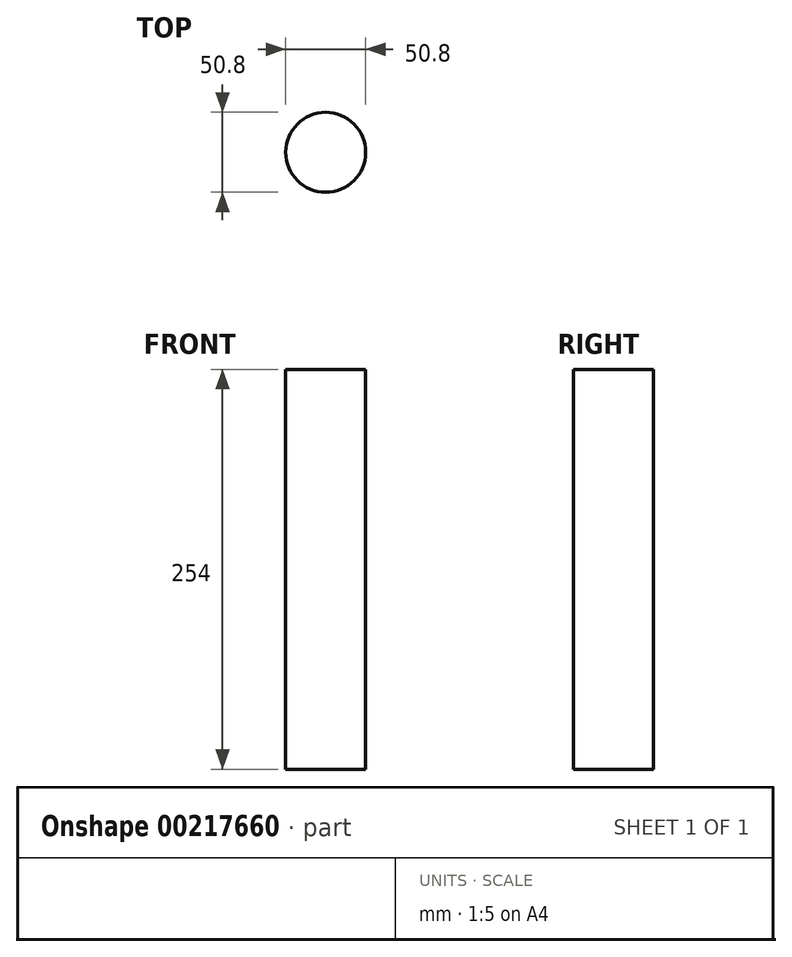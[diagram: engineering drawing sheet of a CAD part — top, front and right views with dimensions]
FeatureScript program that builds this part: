
annotation { "Feature Type Name" : "Feature", "Feature Type Description" : "" }
export const myFeature = defineFeature(function(context is Context, id is Id, definition is map)
    precondition{}
    {
        {
            var Q0;
            Q0=qCreatedBy(makeId("Top.planeOp"),FACE);
            var sketch = newSketch(context, id + "F0", { "sketchPlane" : qUnion([Q0])});
            skCircle(sketch, "E0", {"center": v(0, 0) * mm, "radius": 25.4 * mm});
            skPoint(sketch, "E1", {"position": v(0, 25.4) * mm});
            skPoint(sketch, "E2", {"position": v(0, -25.4) * mm});
            skSolve(sketch);
        }
        {
            var Q0;
            Q0 = qSketchRegion(id + "F0", true);
            extrude(context, id + "F1", {"entities" : qUnion([Q0]), "endBound" : BoundingType.SYMMETRIC, "depth" : 254 * mm});
        }
    });
